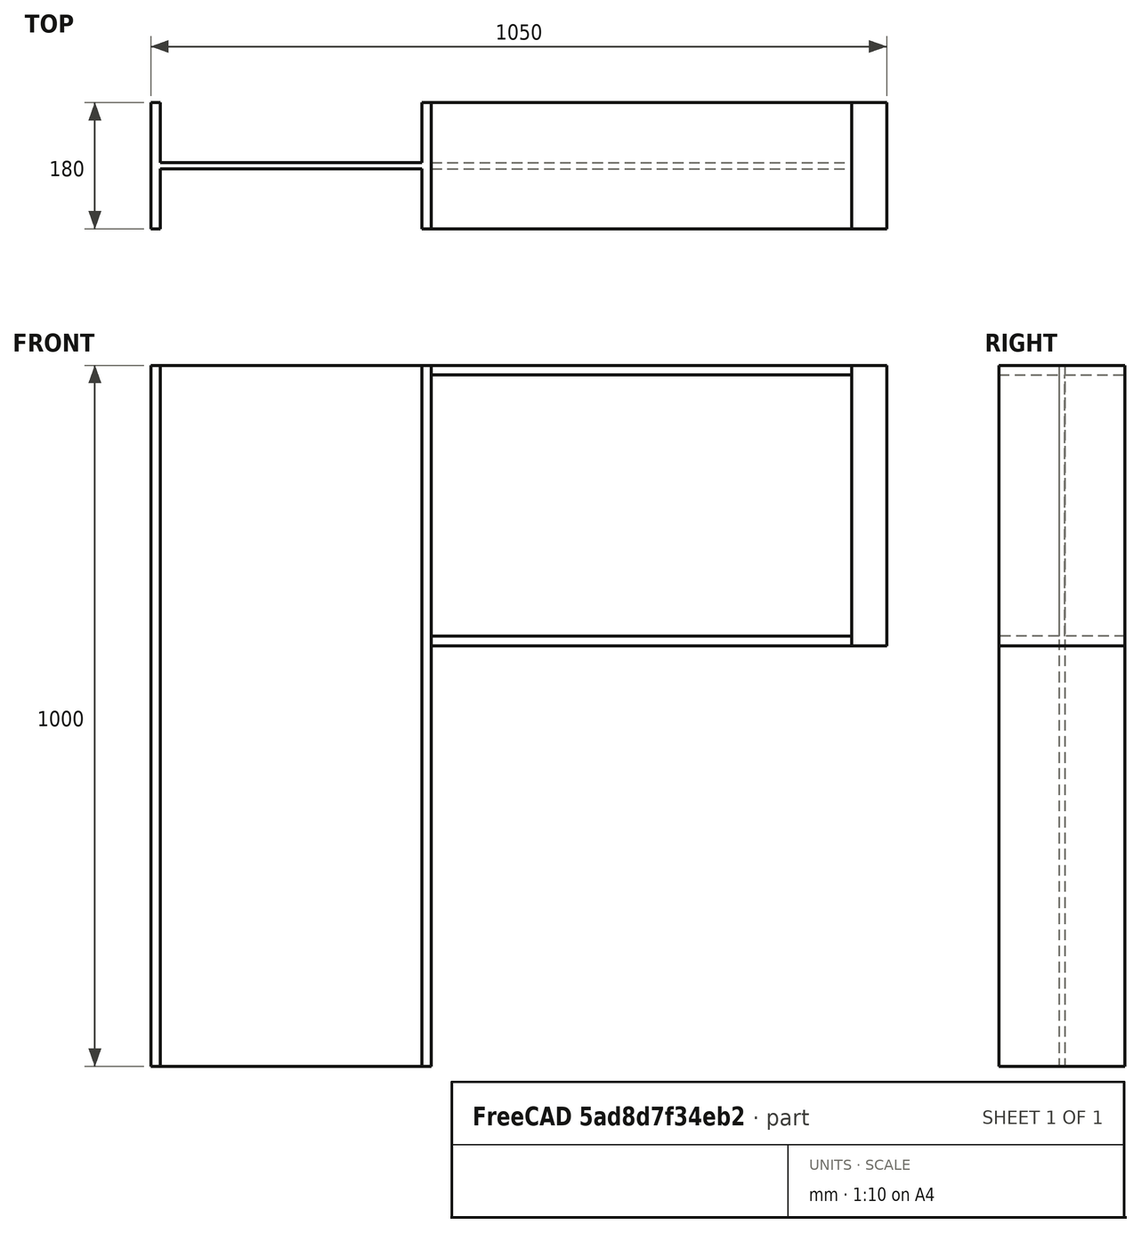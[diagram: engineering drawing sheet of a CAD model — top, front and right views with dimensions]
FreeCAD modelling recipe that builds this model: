
FCSTD DOCUMENT  (FreeCAD 0.21R33771 (Git))
Label: IPE400
License: All rights reserved
LicenseURL: http://en.wikipedia.org/wiki/All_rights_reserved
objects: Sketcher::SketchObject×2, Part::Extrusion×2, Fem::ConstraintForce×2, Part::Box×1, Part::FeaturePython×1, Fem::FemMeshObjectPython×1, Fem::ConstraintFixed×1, App::MaterialObjectPython×1, Fem::FemSolverObjectPython×1, Fem::ConstraintDisplacement×1, Fem::FemAnalysis×1
note: 6 computed .brp shape members not serialized (recipe doc carries the construction recipe); baked Part::Feature solids carry a one-line shape summary decoded from their .brp

FEATURE [Sketcher::SketchObject] Sketch
  FullyConstrained = true
  Placement = pos=(0,0,0) rot=(0.57735,0.57735,0.57735;2.0944rad)
  sketch-geometry (12):
    g0: LineSegment StartX=0 StartY=0 StartZ=0 EndX=180 EndY=0 EndZ=0
    g1: LineSegment StartX=180 StartY=0 StartZ=0 EndX=180 EndY=13.5 EndZ=0
    g2: LineSegment StartX=180 StartY=13.5 StartZ=0 EndX=94.3 EndY=13.5 EndZ=0
    g3: LineSegment StartX=94.3 StartY=13.5 StartZ=0 EndX=94.3 EndY=386.5 EndZ=0
    g4: LineSegment StartX=94.3 StartY=386.5 StartZ=0 EndX=180 EndY=386.5 EndZ=0
    g5: LineSegment StartX=180 StartY=386.5 StartZ=0 EndX=180 EndY=400 EndZ=0
    g6: LineSegment StartX=180 StartY=400 StartZ=0 EndX=0 EndY=400 EndZ=0
    g7: LineSegment StartX=0 StartY=400 StartZ=0 EndX=0 EndY=386.5 EndZ=0
    g8: LineSegment StartX=0 StartY=386.5 StartZ=0 EndX=85.7 EndY=386.5 EndZ=0
    g9: LineSegment StartX=85.7 StartY=386.5 StartZ=0 EndX=85.7 EndY=13.5 EndZ=0
    g10: LineSegment StartX=85.7 StartY=13.5 StartZ=0 EndX=0 EndY=13.5 EndZ=0
    g11: LineSegment StartX=0 StartY=13.5 StartZ=0 EndX=0 EndY=0 EndZ=0
  constraints (35):
    c: Coincident(g-1,g0)
    c: PointOnObject(g0,g-1)
    c: Coincident(g0,g1)
    c: Vertical(g1)
    c: Coincident(g1,g2)
    c: Horizontal(g2)
    c: Coincident(g2,g3)
    c: Vertical(g3)
    c: Coincident(g3,g4)
    c: Horizontal(g4)
    c: Coincident(g4,g5)
    c: Vertical(g5)
    c: Coincident(g5,g6)
    c: Horizontal(g6)
    c: Coincident(g6,g7)
    c: Vertical(g7)
    c: Coincident(g7,g8)
    c: Horizontal(g8)
    c: Coincident(g8,g9)
    c: Vertical(g9)
    c: Coincident(g9,g10)
    c: Horizontal(g10)
    c: Coincident(g10,g11)
    c: Coincident(g11,g0)
    c: DistanceX(g0,g0) = 180
    c: DistanceX(g6,g6) = 180
    c: PointOnObject(g6,g-2)
    c: Vertical(g11)
    c: DistanceX(g2,g2) = 85.7
    c: Equal(g10,g2)
    c: DistanceY(g11,g11) = 13.5
    c: Equal(g11,g1)
    c: Equal(g11,g7)
    c: Equal(g11,g5)
    c: DistanceY(g0,g6) = 400
FEATURE [Part::Extrusion] Extrude
  Base = -> Sketch
  Dir = (1,0,0)
  DirMode = 2
  FaceMakerClass = Part::FaceMakerBullseye
  LengthFwd = 600
  LengthRev = 0
  Solid = true
  Symmetric = false
FEATURE [Sketcher::SketchObject] Sketch001
  FullyConstrained = true
  Placement = pos=(0,0,0) rot=(0.57735,0.57735,0.57735;2.0944rad)
  sketch-geometry (12):
    g0: LineSegment StartX=0 StartY=0 StartZ=0 EndX=180 EndY=0 EndZ=0
    g1: LineSegment StartX=180 StartY=0 StartZ=0 EndX=180 EndY=13.5 EndZ=0
    g2: LineSegment StartX=180 StartY=13.5 StartZ=0 EndX=94.3 EndY=13.5 EndZ=0
    g3: LineSegment StartX=94.3 StartY=13.5 StartZ=0 EndX=94.3 EndY=386.5 EndZ=0
    g4: LineSegment StartX=94.3 StartY=386.5 StartZ=0 EndX=180 EndY=386.5 EndZ=0
    g5: LineSegment StartX=180 StartY=386.5 StartZ=0 EndX=180 EndY=400 EndZ=0
    g6: LineSegment StartX=180 StartY=400 StartZ=0 EndX=0 EndY=400 EndZ=0
    g7: LineSegment StartX=0 StartY=400 StartZ=0 EndX=0 EndY=386.5 EndZ=0
    g8: LineSegment StartX=0 StartY=386.5 StartZ=0 EndX=85.7 EndY=386.5 EndZ=0
    g9: LineSegment StartX=85.7 StartY=386.5 StartZ=0 EndX=85.7 EndY=13.5 EndZ=0
    g10: LineSegment StartX=85.7 StartY=13.5 StartZ=0 EndX=0 EndY=13.5 EndZ=0
    g11: LineSegment StartX=0 StartY=13.5 StartZ=0 EndX=0 EndY=0 EndZ=0
  constraints (35):
    c: Coincident(g-1,g0)
    c: PointOnObject(g0,g-1)
    c: Coincident(g0,g1)
    c: Vertical(g1)
    c: Coincident(g1,g2)
    c: Horizontal(g2)
    c: Coincident(g2,g3)
    c: Vertical(g3)
    c: Coincident(g3,g4)
    c: Horizontal(g4)
    c: Coincident(g4,g5)
    c: Vertical(g5)
    c: Coincident(g5,g6)
    c: Horizontal(g6)
    c: Coincident(g6,g7)
    c: Vertical(g7)
    c: Coincident(g7,g8)
    c: Horizontal(g8)
    c: Coincident(g8,g9)
    c: Vertical(g9)
    c: Coincident(g9,g10)
    c: Horizontal(g10)
    c: Coincident(g10,g11)
    c: Coincident(g11,g0)
    c: DistanceX(g0,g0) = 180
    c: DistanceX(g6,g6) = 180
    c: PointOnObject(g6,g-2)
    c: Vertical(g11)
    c: DistanceX(g2,g2) = 85.7
    c: Equal(g10,g2)
    c: DistanceY(g11,g11) = 13.5
    c: Equal(g11,g1)
    c: Equal(g11,g7)
    c: Equal(g11,g5)
    c: DistanceY(g0,g6) = 400
FEATURE [Part::Extrusion] Extrude001
  Base = -> Sketch001
  Dir = (1,0,0)
  DirMode = 2
  FaceMakerClass = Part::FaceMakerBullseye
  LengthFwd = 1000
  LengthRev = 0
  Placement = pos=(-400,0,400) rot=(0,1,0;1.5708rad)
  Solid = true
  Symmetric = false
FEATURE [Part::Box] Box  label="Cube"
  AttacherType = Attacher::AttachEngine3D
  Height = 400
  Length = 50
  Placement = pos=(600,0,0) rot=(0,0,1;0rad)
  Width = 180
FEATURE [Part::FeaturePython] BooleanFragments  # WARN: FeaturePython — macro-defined, semantics opaque (R4)
  Mode = 2
  Objects = -> [Extrude,Extrude001,Box]
  Tolerance = 0
FEATURE [Fem::FemMeshObjectPython] FEMMeshGmsh  # FEM object (typed FeaturePython)
  Algorithm2D = 0
  Algorithm3D = 0
  CharacteristicLengthMax = 25
  CharacteristicLengthMin = 0
  CoherenceMesh = true
  ElementDimension = 0
  ElementOrder = 1
  GeometryTolerance = 1e-06
  GroupsOfNodes = false
  HighOrderOptimize = 0
  MeshSizeFromCurvature = 12
  OptimizeNetgen = false
  OptimizeStd = true
  Part = -> BooleanFragments
  RecombinationAlgorithm = 0
  Recombine3DAll = false
  RecombineAll = false
  SecondOrderLinear = false
FEATURE [Fem::ConstraintForce] ConstraintForce
  Direction = -> BooleanFragments [Edge81]
  DirectionVector = (1,0,0)
  Force = 1000000
  NormalDirection = (0,0,1)
  Points = (16) [(600,0,400),(616.667,0,400),(633.333,0,400),(650,0,400),(600,60,400),(616.667,60,400),(633.333,60,400),(650,60,400),(600,120,400),(616.667,120,400),+6 more]
  References = -> [BooleanFragments]
  Scale = 11
FEATURE [Fem::ConstraintFixed] ConstraintFixed
  NormalDirection = (0,0,-1)
  Normals = (8) [(0,0,-1),(0,0,-1),(0,0,-1),(0,0,-1),(0,0,-1),(0,0,-1),(0,0,-1),(0,0,-1)]
  Points = (8) [(-400,180,-600),(0,180,-600),(-400,120,-600),(0,120,-600),(-400,60,-600),(0,60,-600),(-400,0,-600),(0,0,-600)]
  References = -> [BooleanFragments]
  Scale = 18
FEATURE [App::MaterialObjectPython] MaterialSolid  # material (typed FeaturePython)
  Category = 0
  Material = AuthorAndLicense=(c) 2014 M. Münch - GNU Lesser General Public License (LGPL),CardName=Steel-15CrNi6,Density=7800 kg/m^3,+16 more (map truncated)
FEATURE [Fem::ConstraintForce] ConstraintForce001
  Direction = -> BooleanFragments [Edge80]
  DirectionVector = (-1,0,0)
  Force = 1000000
  NormalDirection = (0,0,-1)
  Points = (16) [(600,0,0),(616.667,0,0),(633.333,0,0),(650,0,0),(600,60,0),(616.667,60,0),(633.333,60,0),(650,60,0),(600,120,0),(616.667,120,0),(633.333,120,0),+5 more]
  References = -> [BooleanFragments]
  Reversed = true
  Scale = 11
FEATURE [Fem::FemSolverObjectPython] SolverCcxTools  # FEM object (typed FeaturePython)
  AnalysisType = 0
  BeamShellResultOutput3D = false
  BucklingFactors = 1
  EigenmodeHighLimit = 1000000
  EigenmodeLowLimit = 0
  EigenmodesCount = 10
  GeometricalNonlinearity = 0
  IterationsControlParameterCutb = 0.25,0.5,0.75,0.85,,,1.5,
  IterationsControlParameterIter = 4,8,9,200,10,400,,200,,
  IterationsControlParameterTimeUse = false
  IterationsThermoMechMaximum = 2000
  IterationsUserDefinedIncrementations = false
  IterationsUserDefinedTimeStepLength = false
  MaterialNonlinearity = 0
  MatrixSolverType = 0
  SplitInputWriter = false
  ThermoMechSteadyState = true
  TimeEnd = 1
  TimeInitialStep = 0.01
FEATURE [Fem::ConstraintDisplacement] ConstraintDisplacement
  NormalDirection = (0,1,0)
  Normals = (16) [(0,1,0),(0,1,0),(0,1,0),(0,1,0),(0,1,0),(0,1,0),(0,1,0),(0,1,0),(0,1,0),(0,1,0),(0,1,0),(0,1,0),(0,1,0),(0,1,0),(0,1,0),(0,1,0)]
  Points = (16) [(600,180,0),(600,180,133.333),(600,180,266.667),(600,180,400),(616.667,180,0),(616.667,180,133.333),(616.667,180,266.667),(616.667,180,400),+8 more]
  References = -> [BooleanFragments]
  Scale = 16
  hasXFormula = false
  hasYFormula = false
  hasZFormula = false
  rotxFix = false
  rotxFree = true
  rotyFix = false
  rotyFree = true
  rotzFix = false
  rotzFree = true
  useFlowSurfaceForce = false
  xDisplacement = 0
  xFix = false
  xFree = true
  xRotation = 0
  yDisplacement = 0
  yFix = false
  yFree = false
  yRotation = 0
  zDisplacement = 0
  zFix = false
  zFree = true
  zRotation = 0
FEATURE [Fem::FemAnalysis] Analysis
  Group = -> [FEMMeshGmsh,ConstraintForce,ConstraintFixed,MaterialSolid,ConstraintForce001,SolverCcxTools,ConstraintDisplacement]
